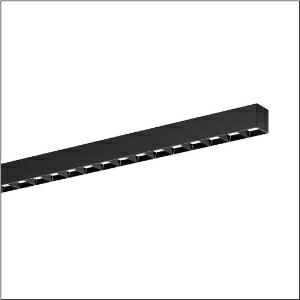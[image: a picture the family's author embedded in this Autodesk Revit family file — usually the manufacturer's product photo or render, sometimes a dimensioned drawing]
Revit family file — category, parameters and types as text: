
# Revit family: silica_r__21_51mx22dc4abb_087a
name_source: partatom
category: Lighting Fixtures
units: mm (PartAtom-declared; Revit-internal decimal feet)

## family parameters
Cut with Voids When Loaded = No
Host = Face
Light Source = No
Part Type = Normal
Room Calculation Point = No
Round Connector Dimension = Use Diameter
Shared = No

## types (1)
- --- (1 x LED, 10800 lm, 64.7 W, 4000K)
    Apparent Load = 65 VA
    CIE Flux Codes = 86 100 100 100 100
    Color Rendering = 80
    Color Temperature = 4000K
    Default Elevation = 1800 mm
    Description = Silica® 21, office luminaire, primary light control with darklight reflector, of PMMA, black, CAT 2 (L<= 3000cd/m²), light emission: direct distribution, primary light characteristic: symmetric, installation type: surface-mounted, LED, rated luminous flux: 10.800lm, luminous efficacy: 167lm/W, light colour: 840, colour temperature: 4000K, with terminal, 3+2-pole, max. 2.5mm², mains connection: 220..240V, AC, 50/60Hz, rated input power: 64.7W, luminaire housing, of aluminium, jet black (RAL 9005), length: 3.004mm, width: 53mm, height: 53mm, protection rating (complete): IP20, insulation class (complete): insulation class I (protective earthing), certification: CE, permissible operating ambient temperature: 0..+35°C, standard: EN 50419, packaging unit: 1 piece
    Height = 0 mm  [stored 0 ft]
    Lamp = 1 x LED
    Lamp Light Flux = 10800 lm
    Lamp Power = 64.7 W
    Lamp count = 1
    Length = 3004 mm
    Luminous efficacy = 167 lm/W
    Manufacturer = Siteco
    ModVariant = No
    Model = 51MX22DC4ABB
    Mounting Place = Ceiling
    Mounting Type = Recessed
    Number of Poles = 1
    OnlyDefault = Yes
    Power Factor = 1
    Product Name = Silica® 21
    Product group = office luminaire | ceiling recessed
    ProductGroupID = 401
    Protection Class = Protection class I
    Protection Degree = IP 20
    RLX_Detail_Level = 1
    RLX_Emergency_Light_Flux = 0 lm
    RLX_Emergency_Type = 0
    RLX_Emergency_Type_DB = No
    RlxData = <blob elided: 64857 chars, md5=71e56082>
    Socket = socket
    Standby Power = 0 W
    System Light Flux = 10800 lm
    System Power = 65 W
    Type Comments = factory setting: luminous flux: 100 % | dim-lin: 254 | 366 mA
    Type Image = l_1313577.jpg
    URL = http://relux.com
    VarID = @adj_074239
    Voltage = 0 V
    Weight = 0.00 kg
    Width = 53 mm

note: [stored X ft] marks values corroborated as IEEE doubles in the binary element streams (Revit-internal decimal feet)

## geometry (parser evidence)
native form markers: Blend x4, Sweep x10
no freeform markers — native parametric forms only
